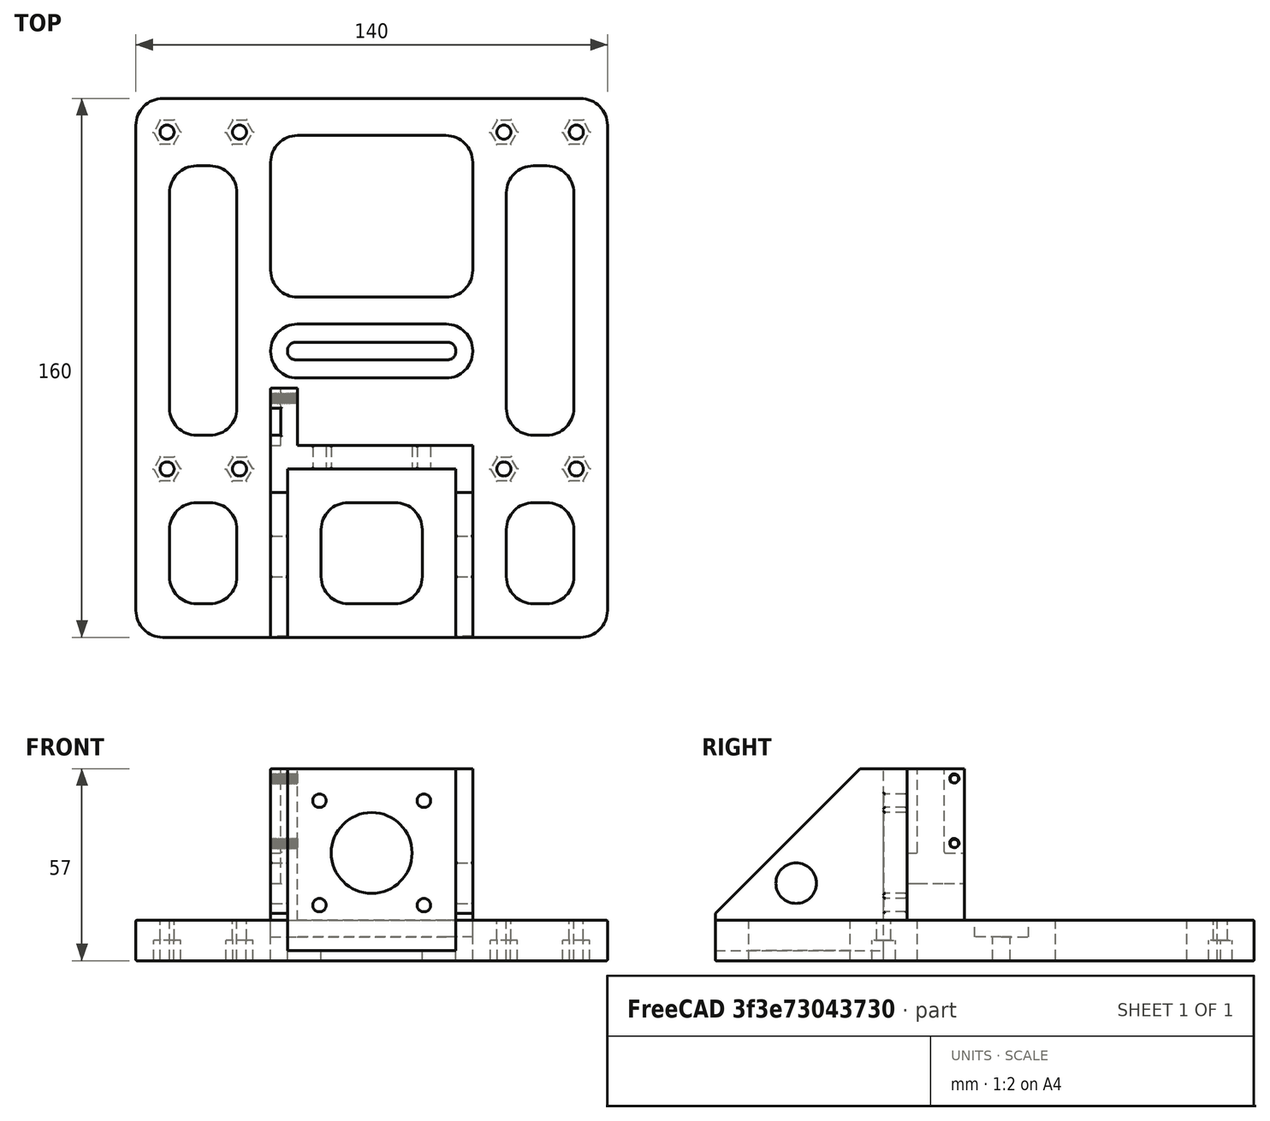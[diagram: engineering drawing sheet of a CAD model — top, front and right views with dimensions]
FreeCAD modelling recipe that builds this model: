
FCSTD DOCUMENT  (FreeCAD 0.18R16131 (Git))
Label: X_Grundplatte_Anfang_Ver2
License: All rights reserved
LicenseURL: http://en.wikipedia.org/wiki/All_rights_reserved
objects: Part::Cut×35, Part::Box×16, Part::Cylinder×14, Part::Fillet×14, Part::Part2DObjectPython×8, Part::Extrusion×8, Part::Feature×2, Part::Chamfer×2, Part::MultiFuse×2
note: 101 computed .brp shape members not serialized (recipe doc carries the construction recipe); baked Part::Feature solids carry a one-line shape summary decoded from their .brp

FEATURE [Part::Box] Box  label="Würfel"
  AttacherType = Attacher::AttachEngine3D
  Height = 12
  Length = 140
  Width = 160
FEATURE [Part::Box] Box002  label="Würfel002"
  AttacherType = Attacher::AttachEngine3D
  Height = 45
  Length = 60
  Placement = pos=(40,50,12) rot=(0,0,1;0rad)
  Width = 7
FEATURE [Part::Cylinder] Cylinder  label="Zylinder"
  Angle = 360
  AttacherType = Attacher::AttachEngine3D
  Height = 20
  Placement = pos=(70,60,32) rot=(1,0,0;1.5708rad)
  Radius = 12
FEATURE [Part::Cylinder] Cylinder001  label="Zylinder001"
  Angle = 360
  AttacherType = Attacher::AttachEngine3D
  Height = 20
  Placement = pos=(85.5,60,16.5) rot=(1,0,0;1.5708rad)
  Radius = 2
FEATURE [Part::Cylinder] Cylinder002  label="Zylinder002"
  Angle = 360
  AttacherType = Attacher::AttachEngine3D
  Height = 20
  Placement = pos=(85.5,60,47.5) rot=(1,0,0;1.5708rad)
  Radius = 2
FEATURE [Part::Cylinder] Cylinder003  label="Zylinder003"
  Angle = 360
  AttacherType = Attacher::AttachEngine3D
  Height = 20
  Placement = pos=(54.5,60,16.5) rot=(1,0,0;1.5708rad)
  Radius = 2
FEATURE [Part::Cylinder] Cylinder004  label="Zylinder004"
  Angle = 360
  AttacherType = Attacher::AttachEngine3D
  Height = 20
  Placement = pos=(54.5,60,47.5) rot=(1,0,0;1.5708rad)
  Radius = 2
FEATURE [Part::Box] Box003  label="Würfel003"
  AttacherType = Attacher::AttachEngine3D
  Height = 45
  Length = 5
  Placement = pos=(40,0,12) rot=(0,0,1;0rad)
  Width = 50
FEATURE [Part::Box] Box004  label="Würfel004"
  AttacherType = Attacher::AttachEngine3D
  Height = 45
  Length = 5
  Placement = pos=(95,0,12) rot=(0,0,1;0rad)
  Width = 50
FEATURE [Part::Box] Box005  label="Würfel005"
  AttacherType = Attacher::AttachEngine3D
  Height = 10
  Length = 50
  Placement = pos=(45,0,3) rot=(0,0,1;0rad)
  Width = 50
FEATURE [Part::Cylinder] Cylinder005  label="Zylinder005"
  Angle = 360
  AttacherType = Attacher::AttachEngine3D
  Height = 80
  Placement = pos=(29,24,23) rot=(0,1,0;1.5708rad)
  Radius = 6
FEATURE [Part::Box] Box007  label="Würfel007"
  AttacherType = Attacher::AttachEngine3D
  Height = 20
  Length = 60
  Placement = pos=(40,101,0) rot=(0,0,1;0rad)
  Width = 48
FEATURE [Part::Box] Box008  label="Würfel008"
  AttacherType = Attacher::AttachEngine3D
  Height = 20
  Length = 20
  Placement = pos=(10,60,0) rot=(0,0,1;0rad)
  Width = 80
FEATURE [Part::Box] Box009  label="Würfel009"
  AttacherType = Attacher::AttachEngine3D
  Height = 20
  Length = 20
  Placement = pos=(110,60,0) rot=(0,0,1;0rad)
  Width = 80
FEATURE [Part::Box] Box010  label="Würfel010"
  AttacherType = Attacher::AttachEngine3D
  Height = 20
  Length = 20
  Placement = pos=(10,10,0) rot=(0,0,1;0rad)
  Width = 30
FEATURE [Part::Box] Box011  label="Würfel011"
  AttacherType = Attacher::AttachEngine3D
  Height = 20
  Length = 20
  Placement = pos=(110,10,0) rot=(0,0,1;0rad)
  Width = 30
FEATURE [Part::Box] Box012  label="Würfel012"
  AttacherType = Attacher::AttachEngine3D
  Height = 10
  Length = 30
  Placement = pos=(55,10,0) rot=(0,0,1;0rad)
  Width = 30
FEATURE [Part::Cylinder] Cylinder006  label="Bohrung001"
  Angle = 360
  AttacherType = Attacher::AttachEngine3D
  Height = 20
  Placement = pos=(9.25,50,0) rot=(0,0,1;0rad)
  Radius = 2.1
FEATURE [Part::Cylinder] Cylinder007  label="Bohrung002"
  Angle = 360
  AttacherType = Attacher::AttachEngine3D
  Height = 20
  Placement = pos=(9.25,150,0) rot=(0,0,1;0rad)
  Radius = 2.1
FEATURE [Part::Cylinder] Cylinder008  label="Bohrung003"
  Angle = 360
  AttacherType = Attacher::AttachEngine3D
  Height = 20
  Placement = pos=(30.75,50,0) rot=(0,0,1;0rad)
  Radius = 2.1
FEATURE [Part::Cylinder] Cylinder009  label="Bohrung004"
  Angle = 360
  AttacherType = Attacher::AttachEngine3D
  Height = 20
  Placement = pos=(30.75,150,0) rot=(0,0,1;0rad)
  Radius = 2.1
FEATURE [Part::Cylinder] Cylinder010  label="Bohrung005"
  Angle = 360
  AttacherType = Attacher::AttachEngine3D
  Height = 20
  Placement = pos=(130.75,150,0) rot=(0,0,1;0rad)
  Radius = 2.1
FEATURE [Part::Cylinder] Cylinder011  label="Bohrung006"
  Angle = 360
  AttacherType = Attacher::AttachEngine3D
  Height = 20
  Placement = pos=(109.25,150,0) rot=(0,0,1;0rad)
  Radius = 2.1
FEATURE [Part::Cylinder] Cylinder012  label="Bohrung007"
  Angle = 360
  AttacherType = Attacher::AttachEngine3D
  Height = 20
  Placement = pos=(109.25,50,0) rot=(0,0,1;0rad)
  Radius = 2.1
FEATURE [Part::Cylinder] Cylinder013  label="Bohrung008"
  Angle = 360
  AttacherType = Attacher::AttachEngine3D
  Height = 20
  Placement = pos=(130.75,50,0) rot=(0,0,1;0rad)
  Radius = 2.1
FEATURE [Part::Part2DObjectPython] Polygon  # Draft 2D object (typed FeaturePython)
  ChamferSize = 0
  DrawMode = 0
  FacesNumber = 6
  FilletRadius = 0
  MakeFace = true
  Radius = 4
FEATURE [Part::Extrusion] Extrude  label="Mutter001"
  Base = -> Polygon
  Dir = (0,0,1)
  DirMode = 2
  FaceMakerClass = Part::FaceMakerBullseye
  LengthFwd = 6
  LengthRev = 0
  Placement = pos=(9.25,50,0) rot=(0,0,1;0rad)
  Solid = false
  Symmetric = false
FEATURE [Part::Part2DObjectPython] Polygon001  # Draft 2D object (typed FeaturePython)
  ChamferSize = 0
  DrawMode = 0
  FacesNumber = 6
  FilletRadius = 0
  MakeFace = true
  Radius = 4
FEATURE [Part::Extrusion] Extrude001  label="Mutter002"
  Base = -> Polygon001
  Dir = (0,0,1)
  DirMode = 2
  FaceMakerClass = Part::FaceMakerBullseye
  LengthFwd = 6
  LengthRev = 0
  Placement = pos=(9.25,150,0) rot=(0,0,1;0rad)
  Solid = false
  Symmetric = false
FEATURE [Part::Part2DObjectPython] Polygon002  # Draft 2D object (typed FeaturePython)
  ChamferSize = 0
  DrawMode = 0
  FacesNumber = 6
  FilletRadius = 0
  MakeFace = true
  Radius = 4
FEATURE [Part::Extrusion] Extrude002  label="Mutter003"
  Base = -> Polygon002
  Dir = (0,0,1)
  DirMode = 2
  FaceMakerClass = Part::FaceMakerBullseye
  LengthFwd = 6
  LengthRev = 0
  Placement = pos=(30.75,50,0) rot=(0,0,1;0rad)
  Solid = false
  Symmetric = false
FEATURE [Part::Part2DObjectPython] Polygon003  # Draft 2D object (typed FeaturePython)
  ChamferSize = 0
  DrawMode = 0
  FacesNumber = 6
  FilletRadius = 0
  MakeFace = true
  Radius = 4
FEATURE [Part::Extrusion] Extrude003  label="Mutter004"
  Base = -> Polygon003
  Dir = (0,0,1)
  DirMode = 2
  FaceMakerClass = Part::FaceMakerBullseye
  LengthFwd = 6
  LengthRev = 0
  Placement = pos=(30.75,150,0) rot=(0,0,1;0rad)
  Solid = false
  Symmetric = false
FEATURE [Part::Part2DObjectPython] Polygon004  # Draft 2D object (typed FeaturePython)
  ChamferSize = 0
  DrawMode = 0
  FacesNumber = 6
  FilletRadius = 0
  MakeFace = true
  Radius = 4
FEATURE [Part::Extrusion] Extrude004  label="Mutter005"
  Base = -> Polygon004
  Dir = (0,0,1)
  DirMode = 2
  FaceMakerClass = Part::FaceMakerBullseye
  LengthFwd = 6
  LengthRev = 0
  Placement = pos=(130.75,50,0) rot=(0,0,1;0rad)
  Solid = false
  Symmetric = false
FEATURE [Part::Part2DObjectPython] Polygon005  # Draft 2D object (typed FeaturePython)
  ChamferSize = 0
  DrawMode = 0
  FacesNumber = 6
  FilletRadius = 0
  MakeFace = true
  Radius = 4
FEATURE [Part::Extrusion] Extrude005  label="Mutter006"
  Base = -> Polygon005
  Dir = (0,0,1)
  DirMode = 2
  FaceMakerClass = Part::FaceMakerBullseye
  LengthFwd = 6
  LengthRev = 0
  Placement = pos=(130.75,150,0) rot=(0,0,1;0rad)
  Solid = false
  Symmetric = false
FEATURE [Part::Part2DObjectPython] Polygon006  # Draft 2D object (typed FeaturePython)
  ChamferSize = 0
  DrawMode = 0
  FacesNumber = 6
  FilletRadius = 0
  MakeFace = true
  Radius = 4
FEATURE [Part::Extrusion] Extrude006  label="Mutter007"
  Base = -> Polygon006
  Dir = (0,0,1)
  DirMode = 2
  FaceMakerClass = Part::FaceMakerBullseye
  LengthFwd = 6
  LengthRev = 0
  Placement = pos=(109.25,150,0) rot=(0,0,1;0rad)
  Solid = false
  Symmetric = false
FEATURE [Part::Part2DObjectPython] Polygon007  # Draft 2D object (typed FeaturePython)
  ChamferSize = 0
  DrawMode = 0
  FacesNumber = 6
  FilletRadius = 0
  MakeFace = true
  Radius = 4
FEATURE [Part::Extrusion] Extrude007  label="Mutter008"
  Base = -> Polygon007
  Dir = (0,0,1)
  DirMode = 2
  FaceMakerClass = Part::FaceMakerBullseye
  LengthFwd = 6
  LengthRev = 0
  Placement = pos=(109.25,50,0) rot=(0,0,1;0rad)
  Solid = false
  Symmetric = false
FEATURE [Part::Cut] Cut
  Base = -> Box
  Tool = -> Cylinder006
FEATURE [Part::Cut] Cut001
  Base = -> Cut
  Tool = -> Extrude007
FEATURE [Part::Cut] Cut002
  Base = -> Cut001
  Tool = -> Extrude006
FEATURE [Part::Cut] Cut003
  Base = -> Cut002
  Tool = -> Extrude005
FEATURE [Part::Cut] Cut004
  Base = -> Cut003
  Tool = -> Extrude004
FEATURE [Part::Cut] Cut005
  Base = -> Cut004
  Tool = -> Extrude003
FEATURE [Part::Cut] Cut006
  Base = -> Cut005
  Tool = -> Extrude002
FEATURE [Part::Cut] Cut007
  Base = -> Cut006
  Tool = -> Extrude001
FEATURE [Part::Cut] Cut008
  Base = -> Cut007
  Tool = -> Extrude
FEATURE [Part::Cut] Cut009
  Base = -> Cut008
  Tool = -> Cylinder013
FEATURE [Part::Cut] Cut010
  Base = -> Cut009
  Tool = -> Cylinder012
FEATURE [Part::Cut] Cut011
  Base = -> Cut010
  Tool = -> Cylinder011
FEATURE [Part::Cut] Cut012
  Base = -> Cut011
  Tool = -> Cylinder010
FEATURE [Part::Cut] Cut013
  Base = -> Cut012
  Tool = -> Cylinder009
FEATURE [Part::Cut] Cut014
  Base = -> Cut013
  Tool = -> Cylinder008
FEATURE [Part::Cut] Cut015
  Base = -> Cut014
  Tool = -> Cylinder007
FEATURE [Part::Fillet] Fillet
  Base = -> Box008
  Edges = 4 edges r=8: [Edge1,Edge3,Edge5,Edge7]
FEATURE [Part::Fillet] Fillet001
  Base = -> Box010
  Edges = 4 edges r=8: [Edge1,Edge3,Edge5,Edge7]
FEATURE [Part::Fillet] Fillet002
  Base = -> Box009
  Edges = 4 edges r=8: [Edge1,Edge3,Edge5,Edge7]
FEATURE [Part::Fillet] Fillet003
  Base = -> Box011
  Edges = 4 edges r=8: [Edge1,Edge3,Edge5,Edge7]
FEATURE [Part::Cut] Cut016
  Base = -> Cut015
  Tool = -> Fillet003
FEATURE [Part::Cut] Cut017
  Base = -> Cut016
  Tool = -> Fillet002
FEATURE [Part::Cut] Cut018
  Base = -> Cut017
  Tool = -> Fillet001
FEATURE [Part::Box] Box013  label="Würfel013"
  AttacherType = Attacher::AttachEngine3D
  Height = 20
  Length = 60
  Placement = pos=(40,77,7) rot=(0,0,1;0rad)
  Width = 16
FEATURE [Part::Fillet] Fillet004
  Base = -> Box013
  Edges = 4 edges r=7.9: [Edge1,Edge3,Edge5,Edge7]
FEATURE [Part::Box] Box014  label="Würfel014"
  AttacherType = Attacher::AttachEngine3D
  Height = 20
  Length = 50
  Placement = pos=(45,82.4,0) rot=(0,0,1;0rad)
  Width = 5.2
FEATURE [Part::Fillet] Fillet005
  Base = -> Box014
  Edges = 4 edges r=2.5: [Edge1,Edge3,Edge5,Edge7]
FEATURE [Part::Fillet] Fillet006
  Base = -> Box007
  Edges = 4 edges r=8: [Edge1,Edge3,Edge5,Edge7]
FEATURE [Part::Box] Box015  label="Würfel015"
  AttacherType = Attacher::AttachEngine3D
  Height = 57
  Length = 8
  Placement = pos=(40,57,0) rot=(0,0,1;0rad)
  Width = 17
FEATURE [Part::Cut] Cut019
  Base = -> Cut018
  Tool = -> Fillet
FEATURE [Part::Cut] Cut020
  Base = -> Cut019
  Tool = -> Fillet004
FEATURE [Part::Cut] Cut021
  Base = -> Cut020
  Tool = -> Fillet005
FEATURE [Part::Cut] Cut022
  Base = -> Cut021
  Tool = -> Fillet006
FEATURE [Part::Feature] Part__Feature  label="ScrewTap-M3x30_"
  Placement = pos=(28,71,54) rot=(0,1,0;-1.5708rad)
  shape: bbox 31.5 x 4.617 x 4.303 mm, 250 faces (baked)
FEATURE [Part::Feature] Part__Feature001  label="ScrewTap-M3x30_001"
  Placement = pos=(28,71,34.8) rot=(0,-1,0;1.5708rad)
  shape: bbox 31.5 x 4.617 x 4.303 mm, 250 faces (baked)
FEATURE [Part::Box] Box016  label="Würfel016"
  AttacherType = Attacher::AttachEngine3D
  Height = 57
  Length = 3
  Placement = pos=(40,60,23) rot=(0,0,1;0rad)
  Width = 8
FEATURE [Part::Box] Box017  label="Würfel017"
  AttacherType = Attacher::AttachEngine3D
  Height = 9
  Length = 3
  Placement = pos=(40,57,23) rot=(0,0,1;0rad)
  Width = 17
FEATURE [Part::Cut] Cut023
  Base = -> Box015
  Tool = -> Box016
FEATURE [Part::Cut] Cut024
  Base = -> Cut023
  Tool = -> Box017
FEATURE [Part::Cut] Cut025
  Base = -> Cut024
  Tool = -> Part__Feature001
FEATURE [Part::Cut] Cut026
  Base = -> Cut025
  Tool = -> Part__Feature
FEATURE [Part::Cut] Cut027
  Base = -> Box002
  Tool = -> Cylinder
FEATURE [Part::Cut] Cut028
  Base = -> Cut027
  Tool = -> Cylinder001
FEATURE [Part::Cut] Cut029
  Base = -> Cut028
  Tool = -> Cylinder002
FEATURE [Part::Cut] Cut030
  Base = -> Cut029
  Tool = -> Cylinder003
FEATURE [Part::Cut] Cut031
  Base = -> Cut030
  Tool = -> Cylinder004
FEATURE [Part::Fillet] Fillet007
  Base = -> Cut031
  Edges = 10 edges r=0.5: [Edge8,Edge9,Edge10,Edge11,Edge12,Edge17,Edge18,Edge19,Edge20,Edge21]
FEATURE [Part::Chamfer] Chamfer
  Base = -> Box004
  Edges = 1 edges r=43: [Edge10]
FEATURE [Part::Chamfer] Chamfer001
  Base = -> Box003
  Edges = 1 edges r=43: [Edge10]
FEATURE [Part::Cut] Cut032
  Base = -> Cut022
  Tool = -> Box005
FEATURE [Part::Fillet] Fillet008
  Base = -> Box012
  Edges = 4 edges r=8: [Edge1,Edge3,Edge5,Edge7]
FEATURE [Part::Cut] Cut033
  Base = -> Cut032
  Tool = -> Fillet008
FEATURE [Part::MultiFuse] Fusion
  Shapes = -> [Cut026,Chamfer001,Fillet007,Chamfer]
FEATURE [Part::Cut] Cut034
  Base = -> Fusion
  Tool = -> Cylinder005
FEATURE [Part::Fillet] Fillet009
  Base = -> Cut033
  Edges = 4 edges r=8: [Edge1,Edge3,Edge5,Edge74]
FEATURE [Part::Fillet] Fillet010
  Base = -> Fillet009
  Edges = 119 edges r=0.3: [Edge4,Edge72,Edge74,Edge76,Edge77,Edge78,Edge79,Edge80,Edge81,Edge82,Edge83,Edge84,Edge85,Edge86,Edge87,Edge88,Edge89,Edge90,Edge91,Edge92,Edge93,Edge94,Edge95,Edge96,Edge97,Edge98,Edge99,Edge100,Edge101,Edge102,Edge103,Edge104,Edge105,Edge106,Edge107,Edge108,Edge109,Edge110,Edge111,Edge112,Edge113,+78 more]
FEATURE [Part::Fillet] Fillet011
  Base = -> Fillet010
  Edges = 81 edges r=0.3: [Edge3,Edge6,Edge11,Edge12,Edge13,Edge14,Edge15,Edge16,Edge17,Edge21,Edge22,Edge23,Edge24,Edge25,Edge26,Edge27,Edge28,Edge29,Edge30,Edge31,Edge32,Edge33,Edge34,Edge35,Edge36,Edge37,Edge38,Edge39,Edge40,Edge41,Edge42,Edge43,Edge44,Edge45,Edge46,Edge47,Edge48,Edge49,Edge50,Edge51,Edge52,Edge53,Edge54,+38 more]
FEATURE [Part::MultiFuse] Fusion001
  Shapes = -> [Cut034,Fillet011]
FEATURE [Part::Fillet] Fillet012
  Base = -> Fusion001
  Edges = 4 edges r=0.5: [Edge65,Edge202,Edge227,Edge390]
FEATURE [Part::Fillet] Fillet013
  Base = -> Fillet012
  Edges = 19 edges r=0.3: [Edge146,Edge147,Edge148,Edge149,Edge150,Edge151,Edge152,Edge153,Edge272,Edge273,Edge274,Edge326,Edge327,Edge328,Edge329,Edge346,Edge347,Edge357,Edge478]
